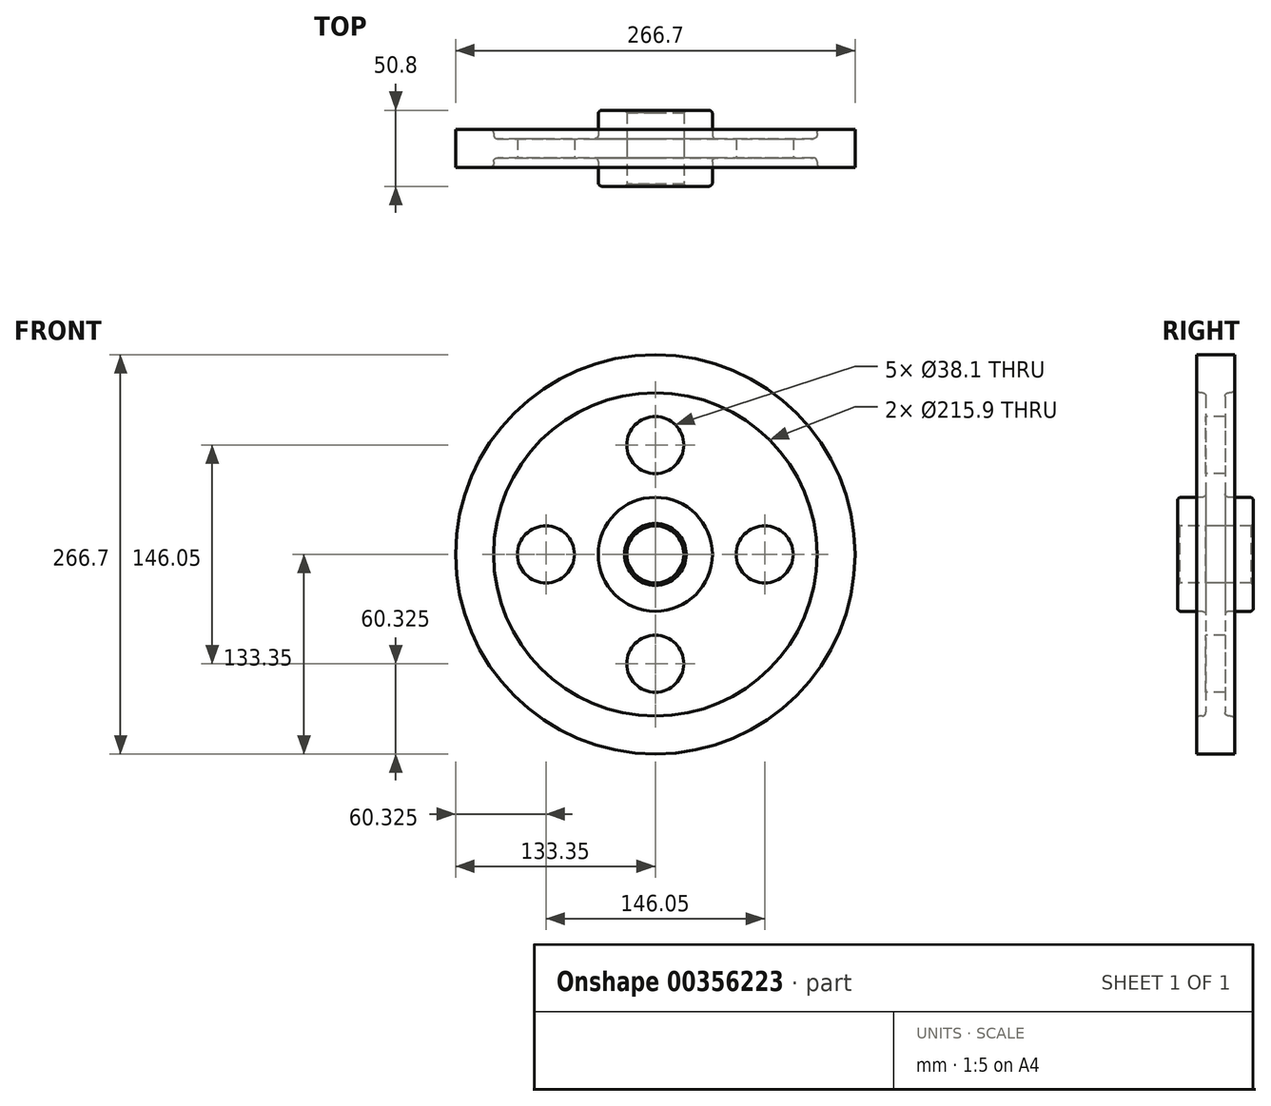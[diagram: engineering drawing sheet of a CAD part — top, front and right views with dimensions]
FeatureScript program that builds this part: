
annotation { "Feature Type Name" : "Feature", "Feature Type Description" : "" }
export const myFeature = defineFeature(function(context is Context, id is Id, definition is map)
    precondition{}
    {
        {
            var Q0;
            Q0=qCreatedBy(makeId("Right.planeOp"),FACE);
            var sketch = newSketch(context, id + "F0", { "sketchPlane" : qUnion([Q0])});
            skLineSegment(sketch, "E0", {"start": v(0, 0) * mm, "end": v(25.4, 0) * mm});
            skLineSegment(sketch, "E1.0", {"start": v(0, 19.05) * mm, "end": v(25.4, 19.05) * mm});
            skLineSegment(sketch, "E2.0", {"start": v(6.35, 38.1) * mm, "end": v(25.4, 38.1) * mm});
            skLineSegment(sketch, "E3.0", {"start": v(6.35, 107.95) * mm, "end": v(12.7, 107.95) * mm});
            skLineSegment(sketch, "E4.0", {"start": v(0, 133.35) * mm, "end": v(12.7, 133.35) * mm});
            skLineSegment(sketch, "E5", {"start": v(0, 133.35) * mm, "end": v(0, 19.05) * mm});
            skLineSegment(sketch, "E6.0", {"start": v(25.4, 38.1) * mm, "end": v(25.4, 19.05) * mm});
            skLineSegment(sketch, "E7.0", {"start": v(6.35, 107.95) * mm, "end": v(6.35, 38.1) * mm});
            skLineSegment(sketch, "E8.0", {"start": v(12.7, 133.35) * mm, "end": v(12.7, 107.95) * mm});
            skLineSegment(sketch, "E9.MirrorCS", {"start": v(0, 133.35) * mm, "end": v(-12.7, 133.35) * mm});
            skLineSegment(sketch, "E10.MirrorCS", {"start": v(-12.7, 133.35) * mm, "end": v(-12.7, 107.95) * mm});
            skLineSegment(sketch, "E11.MirrorCS", {"start": v(-6.35, 107.95) * mm, "end": v(-6.35, 38.1) * mm});
            skLineSegment(sketch, "E12.MirrorCS", {"start": v(-6.35, 38.1) * mm, "end": v(-25.4, 38.1) * mm});
            skLineSegment(sketch, "E13.MirrorCS", {"start": v(-6.35, 107.95) * mm, "end": v(-12.7, 107.95) * mm});
            skLineSegment(sketch, "E14.MirrorCS", {"start": v(-25.4, 38.1) * mm, "end": v(-25.4, 19.05) * mm});
            skLineSegment(sketch, "E15.MirrorCS", {"start": v(0, 19.05) * mm, "end": v(-25.4, 19.05) * mm});
            skSolve(sketch);
        }
        {
            var Q0;
            Q0=makeQuery(id+"F0.imprint","IMPRINT",FACE,{"disambiguationData":[TD([[makeQuery(id+"F0.imprint","IMPRINT",EDGE,{"derivedFrom":sQuery(id+"F0.wireOp",EDGE,"E5")}),-1.0]])]});
            var Q1;
            Q1=makeQuery(id+"F0.imprint","IMPRINT",FACE,{"disambiguationData":[TD([[makeQuery(id+"F0.imprint","IMPRINT",EDGE,{"derivedFrom":sQuery(id+"F0.wireOp",EDGE,"E1.0")}),1.0]])]});
            var Q2;
            Q2=sQuery(id+"F0.wireOp",EDGE,"E0");
            revolve(context, id + "F1", {"entities" : qUnion([Q0, Q1]), "axis" : qUnion([Q2]), "revolveType" : RevolveType.FULL});
        }
        {
            var Q0;
            Q0=makeQuery(id+"F1.opRevolve","SWEPT_FACE",FACE,{"disambiguationData":[OSD([sQuery(id+"F0.wireOp",EDGE,"E11.MirrorCS")])]});
            var sketch = newSketch(context, id + "F2", { "sketchPlane" : qUnion([Q0])});
            skLineSegment(sketch, "E16", {"start": v(0, 0) * mm, "end": v(0, 73.03) * mm});
            skCircle(sketch, "E17", {"center": v(0, 73.03) * mm, "radius": 19.05 * mm});
            skCircle(sketch, "E18.1.0", {"center": v(-73.03, 0) * mm, "radius": 19.05 * mm});
            skCircle(sketch, "E18.2.0", {"center": v(0, -73.03) * mm, "radius": 19.05 * mm});
            skCircle(sketch, "E18.3.0", {"center": v(73.03, 0) * mm, "radius": 19.05 * mm});
            skPoint(sketch, "E18.center", {"position": v(0, 0) * mm});
            skSolve(sketch);
        }
        {
            var Q0;
            Q0=makeQuery(id+"F2.imprint","IMPRINT",FACE,{"disambiguationData":[TD([[makeQuery(id+"F2.imprint","IMPRINT",EDGE,{"derivedFrom":sQuery(id+"F2.wireOp",EDGE,"E17")}),1.0]])]});
            var Q1;
            Q1=makeQuery(id+"F2.imprint","IMPRINT",FACE,{"disambiguationData":[TD([[makeQuery(id+"F2.imprint","IMPRINT",EDGE,{"derivedFrom":sQuery(id+"F2.wireOp",EDGE,"E18.1.0")}),1.0]])]});
            var Q2;
            Q2=makeQuery(id+"F2.imprint","IMPRINT",FACE,{"disambiguationData":[TD([[makeQuery(id+"F2.imprint","IMPRINT",EDGE,{"derivedFrom":sQuery(id+"F2.wireOp",EDGE,"E18.2.0")}),1.0]])]});
            var Q3;
            Q3=makeQuery(id+"F2.imprint","IMPRINT",FACE,{"disambiguationData":[TD([[makeQuery(id+"F2.imprint","IMPRINT",EDGE,{"derivedFrom":sQuery(id+"F2.wireOp",EDGE,"E18.3.0")}),1.0]])]});
            extrude(context, id + "F3", {"entities" : qUnion([Q0, Q1, Q2, Q3]), "operationType" : NewBodyOperationType.REMOVE, "oppositeDirection" : true, "depth" : 25.4 * mm});
        }
        {
            var Q0;
            Q0=makeQuery(id+"F1.opRevolve","SWEPT_EDGE",EDGE,{"disambiguationData":[OSD([sQuery(id+"F0.wireOp",EDGE,"E11.MirrorCS"),sQuery(id+"F0.wireOp",EDGE,"E13.MirrorCS")])]});
            var Q1;
            Q1=makeQuery(id+"F1.opRevolve","SWEPT_EDGE",EDGE,{"disambiguationData":[OSD([sQuery(id+"F0.wireOp",EDGE,"E10.MirrorCS"),sQuery(id+"F0.wireOp",EDGE,"E13.MirrorCS")])]});
            var Q2;
            Q2=makeQuery(id+"F1.opRevolve","SWEPT_FACE",FACE,{"disambiguationData":[OSD([sQuery(id+"F0.wireOp",EDGE,"E12.MirrorCS")])]});
            var Q3;
            Q3=makeQuery(id+"F1.opRevolve","SWEPT_EDGE",EDGE,{"disambiguationData":[OSD([sQuery(id+"F0.wireOp",EDGE,"E12.MirrorCS"),sQuery(id+"F0.wireOp",EDGE,"E14.MirrorCS")])]});
            var Q4;
            Q4=makeQuery(id+"F1.opRevolve","SWEPT_EDGE",EDGE,{"disambiguationData":[OSD([sQuery(id+"F0.wireOp",EDGE,"E2.0"),sQuery(id+"F0.wireOp",EDGE,"E6.0")])]});
            var Q5;
            Q5=makeQuery(id+"F1.opRevolve","SWEPT_EDGE",EDGE,{"disambiguationData":[OSD([sQuery(id+"F0.wireOp",EDGE,"E2.0"),sQuery(id+"F0.wireOp",EDGE,"E7.0")])]});
            var Q6;
            Q6=makeQuery(id+"F1.opRevolve","SWEPT_EDGE",EDGE,{"disambiguationData":[OSD([sQuery(id+"F0.wireOp",EDGE,"E3.0"),sQuery(id+"F0.wireOp",EDGE,"E8.0")])]});
            var Q7;
            Q7=makeQuery(id+"F1.opRevolve","SWEPT_EDGE",EDGE,{"disambiguationData":[OSD([sQuery(id+"F0.wireOp",EDGE,"E3.0"),sQuery(id+"F0.wireOp",EDGE,"E7.0")])]});
            fillet(context, id + "F4", {"entities" : qUnion([Q0, Q1, Q2, Q3, Q4, Q5, Q6, Q7]), "radius" : 2.54 * mm, "tangentPropagation" : true, "allowEdgeOverflow" : false});
        }
        {
            var Q0;
            Q0=makeQuery(id+"F1.opRevolve","SWEPT_EDGE",EDGE,{"disambiguationData":[OSD([sQuery(id+"F0.wireOp",EDGE,"E14.MirrorCS"),sQuery(id+"F0.wireOp",EDGE,"E15.MirrorCS")])]});
            var Q1;
            Q1=makeQuery(id+"F1.opRevolve","SWEPT_EDGE",EDGE,{"disambiguationData":[OSD([sQuery(id+"F0.wireOp",EDGE,"E1.0"),sQuery(id+"F0.wireOp",EDGE,"E6.0")])]});
            chamfer(context, id + "F5", {"entities" : qUnion([Q0, Q1]), "width" : 1.59 * mm, "tangentPropagation" : true});
        }
    });
